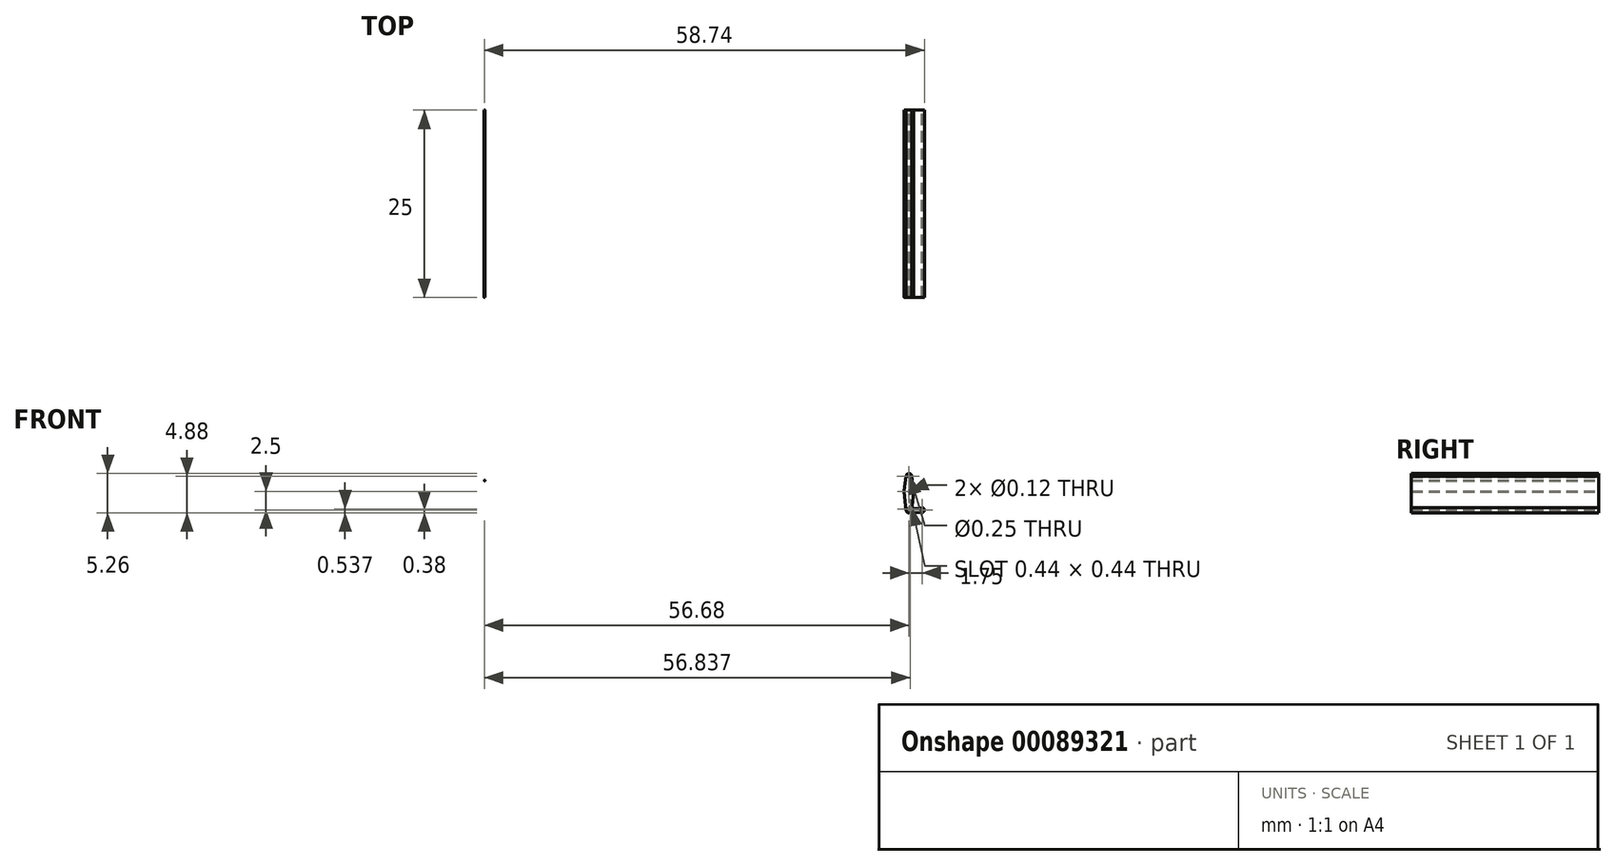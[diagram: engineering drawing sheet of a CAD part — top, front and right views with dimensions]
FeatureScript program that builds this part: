
annotation { "Feature Type Name" : "Feature", "Feature Type Description" : "" }
export const myFeature = defineFeature(function(context is Context, id is Id, definition is map)
    precondition{}
    {
        {
            var Q0;
            Q0=qCreatedBy(makeId("Front.planeOp"),FACE);
            var sketch = newSketch(context, id + "F0", { "sketchPlane" : qUnion([Q0])});
            skCircle(sketch, "E0", {"center": v(0, 2) * mm, "radius": 0.38 * mm});
            skCircle(sketch, "E1", {"center": v(0, 2) * mm, "radius": 0.12 * mm});
            skLineSegment(sketch, "E2", {"start": v(0, 2) * mm, "end": v(0, 0) * mm});
            skCircle(sketch, "E3", {"center": v(0, 0) * mm, "radius": 0.62 * mm});
            skLineSegment(sketch, "E4", {"start": v(0, 0) * mm, "end": v(0, -2.5) * mm});
            skCircle(sketch, "E5", {"center": v(0, -2.5) * mm, "radius": 0.38 * mm});
            skLineSegment(sketch, "E6", {"start": v(0, -2.5) * mm, "end": v(1.75, -2.5) * mm});
            skCircle(sketch, "E7", {"center": v(1.75, -2.5) * mm, "radius": 0.31 * mm});
            skCircle(sketch, "E8", {"center": v(-56.62, 1.44) * mm, "radius": 0.06 * mm});
            skCircle(sketch, "E9", {"center": v(0, 0) * mm, "radius": 0.06 * mm});
            skCircle(sketch, "E10", {"center": v(0, -2.5) * mm, "radius": 0.06 * mm});
            skCircle(sketch, "E11", {"center": v(1.75, -2.5) * mm, "radius": 0.06 * mm});
            skLineSegment(sketch, "E12", {"start": v(0.37, 1.98) * mm, "end": v(0.62, 0.08) * mm});
            skLineSegment(sketch, "E13", {"start": v(-0.37, 1.98) * mm, "end": v(-0.62, 0.08) * mm});
            skLineSegment(sketch, "E14", {"start": v(-0.62, -0.06) * mm, "end": v(-0.37, -2.54) * mm});
            skLineSegment(sketch, "E15", {"start": v(0.62, -0.06) * mm, "end": v(0.43, -1.97) * mm});
            skLineSegment(sketch, "E16", {"start": v(0.78, -2.32) * mm, "end": v(1.7, -2.2) * mm});
            skLineSegment(sketch, "E17", {"start": v(0.01, -2.87) * mm, "end": v(1.76, -2.81) * mm});
            skArc(sketch, "E18.filletArc", {"start": v(0.43, -1.97) * mm, "mid": v(0.52, -2.23) * mm, "end": v(0.78, -2.32) * mm});
            skSolve(sketch);
        }
        {
            var Q0;
            Q0 = qSketchRegion(id + "F0", true);
            extrude(context, id + "F1", {"entities" : qUnion([Q0]), "depth" : 25 * mm});
        }
    });
